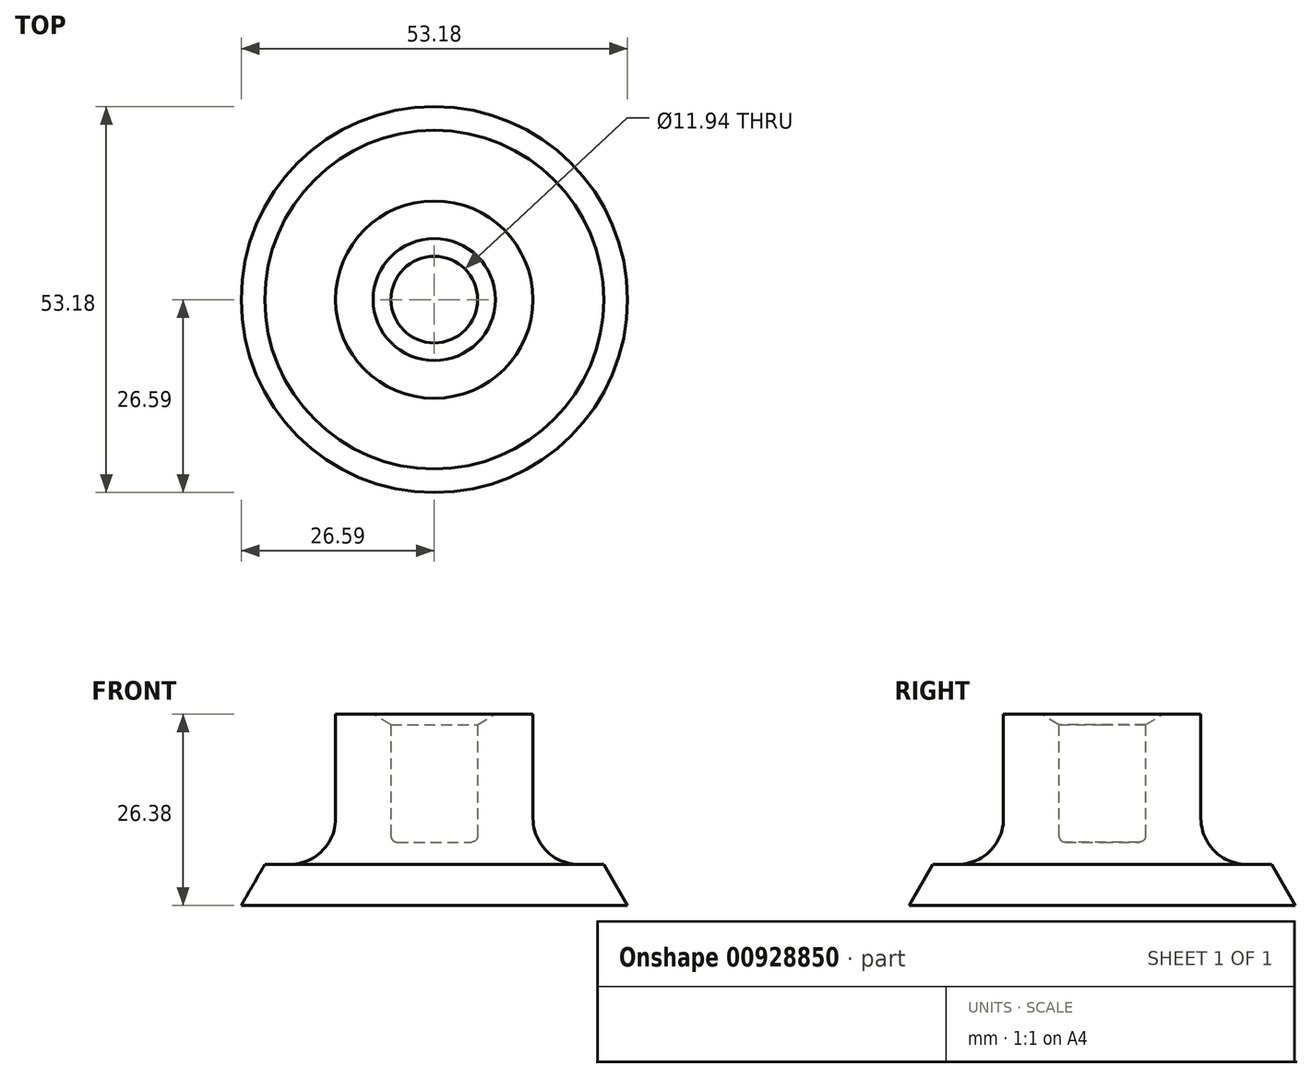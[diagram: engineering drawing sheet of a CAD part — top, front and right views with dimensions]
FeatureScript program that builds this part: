
annotation { "Feature Type Name" : "Feature", "Feature Type Description" : "" }
export const myFeature = defineFeature(function(context is Context, id is Id, definition is map)
    precondition{}
    {
        {
            var Q0;
            Q0=qCreatedBy(makeId("Front.planeOp"),FACE);
            var sketch = newSketch(context, id + "F0", { "sketchPlane" : qUnion([Q0])});
            skLineSegment(sketch, "E0", {"start": v(0, 0) * mm, "end": v(0, 24.9) * mm, "construction": true});
            skLineSegment(sketch, "E1", {"start": v(-5.97, 24.9) * mm, "end": v(-5.97, 9.6) * mm});
            skLineSegment(sketch, "E2", {"start": v(-5.1, 8.73) * mm, "end": v(0, 8.73) * mm});
            skLineSegment(sketch, "E3", {"start": v(-5.97, 24.9) * mm, "end": v(-8.41, 26.38) * mm});
            skLineSegment(sketch, "E4", {"start": v(-8.41, 26.38) * mm, "end": v(-13.59, 26.38) * mm});
            skLineSegment(sketch, "E5", {"start": v(-13.59, 26.38) * mm, "end": v(-13.59, 12) * mm});
            skLineSegment(sketch, "E6", {"start": v(-19.94, 5.65) * mm, "end": v(-23.33, 5.65) * mm});
            skLineSegment(sketch, "E7", {"start": v(-23.33, 5.65) * mm, "end": v(-26.6, 0) * mm});
            skLineSegment(sketch, "E8", {"start": v(-26.6, 0) * mm, "end": v(0, 0) * mm});
            skArc(sketch, "E9.filletArc", {"start": v(-19.94, 5.65) * mm, "mid": v(-15.45, 7.51) * mm, "end": v(-13.59, 12) * mm});
            skArc(sketch, "E10.filletArc", {"start": v(-5.97, 9.6) * mm, "mid": v(-5.72, 8.99) * mm, "end": v(-5.1, 8.73) * mm});
            skLineSegment(sketch, "E11", {"start": v(0, 8.73) * mm, "end": v(0, 0) * mm});
            skSolve(sketch);
        }
        {
            var Q0;
            Q0=makeQuery(id+"F0.imprint","IMPRINT",FACE,{"disambiguationData":[TD([[makeQuery(id+"F0.imprint","IMPRINT",EDGE,{"derivedFrom":sQuery(id+"F0.wireOp",EDGE,"E1")}),-1.0]])]});
            var Q1;
            Q1=sQuery(id+"F0.wireOp",EDGE,"E0");
            revolve(context, id + "F1", {"surfaceOperationType" : NewSurfaceOperationType.NEW, "entities" : qUnion([Q0]), "axis" : qUnion([Q1]), "revolveType" : RevolveType.FULL});
        }
    });
